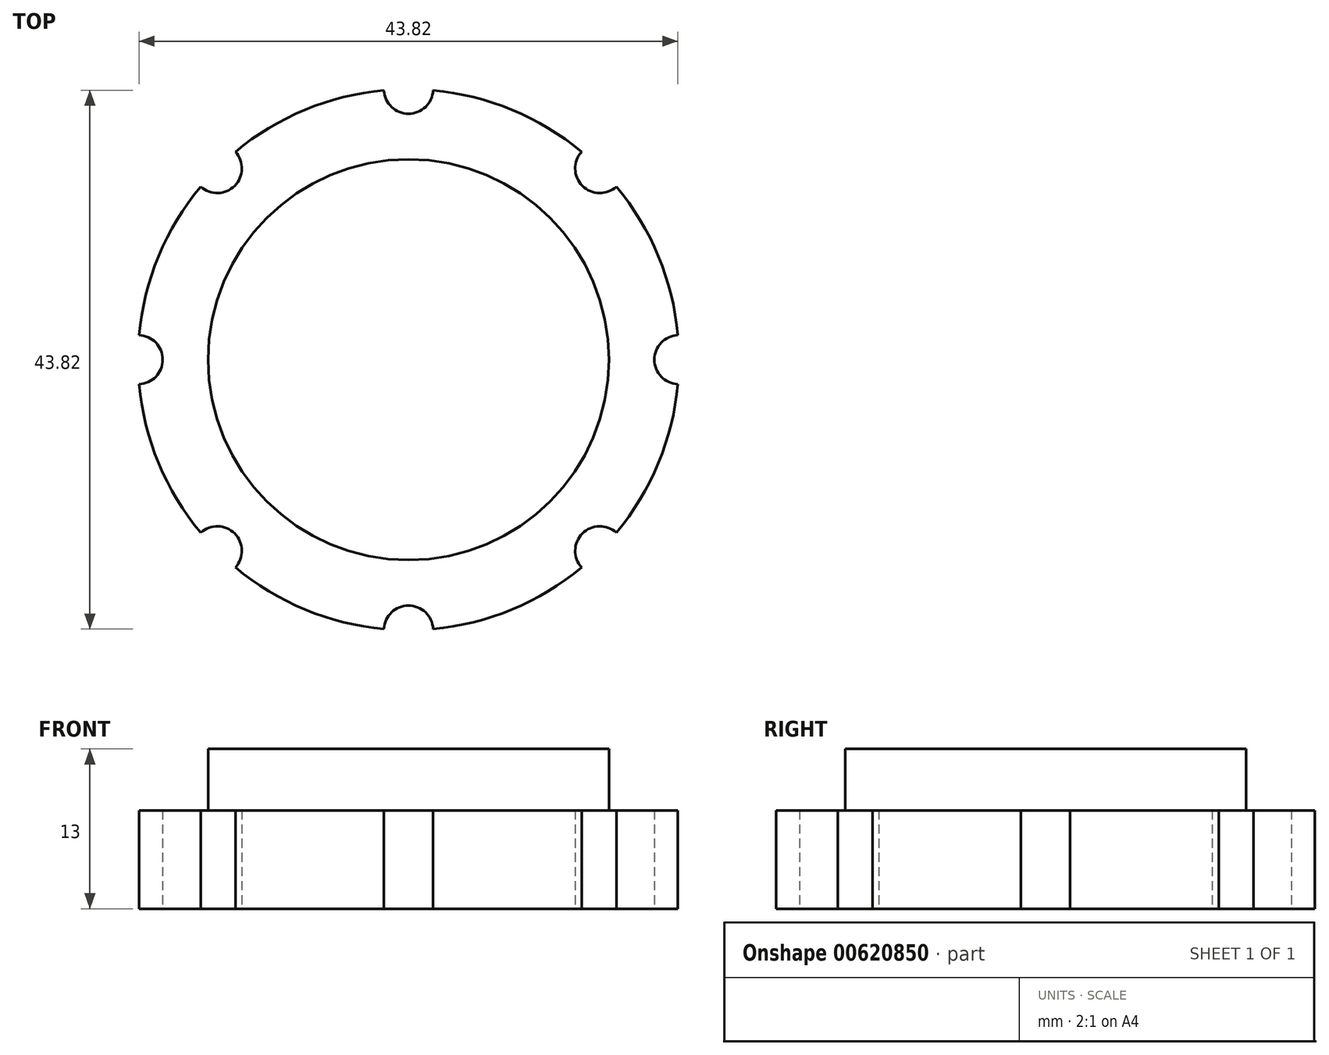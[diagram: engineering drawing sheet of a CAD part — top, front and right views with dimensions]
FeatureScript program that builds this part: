
annotation { "Feature Type Name" : "Feature", "Feature Type Description" : "" }
export const myFeature = defineFeature(function(context is Context, id is Id, definition is map)
    precondition{}
    {
        {
            var Q0;
            Q0=qCreatedBy(makeId("Top.planeOp"),FACE);
            var sketch = newSketch(context, id + "F0", { "sketchPlane" : qUnion([Q0])});
            skCircle(sketch, "E0", {"center": v(0, 0) * mm, "radius": 22 * mm});
            skSolve(sketch);
        }
        {
            var Q0;
            Q0 = qSketchRegion(id + "F0", true);
            extrude(context, id + "F1", {"entities" : qUnion([Q0]), "depth" : 8 * mm, "offsetDistance" : 25 * mm});
        }
        {
            var Q0;
            Q0=makeQuery(id+"F1.opExtrude","CAP_FACE",FACE,{"disambiguationData":[OSD([sQuery(id+"F0.wireOp",EDGE,"E0")])],"isStart":false});
            var sketch = newSketch(context, id + "F2", { "sketchPlane" : qUnion([Q0])});
            skCircle(sketch, "E1", {"center": v(0, 0) * mm, "radius": 16.3 * mm});
            skSolve(sketch);
        }
        {
            var Q0;
            Q0 = qSketchRegion(id + "F2", true);
            extrude(context, id + "F3", {"entities" : qUnion([Q0]), "operationType" : NewBodyOperationType.ADD, "depth" : 5 * mm, "offsetDistance" : 25 * mm});
        }
        {
            var Q0;
            Q0=makeQuery(id+"F1.opExtrude","CAP_FACE",FACE,{"disambiguationData":[OSD([sQuery(id+"F0.wireOp",EDGE,"E0")])],"isStart":true});
            var sketch = newSketch(context, id + "F4", { "sketchPlane" : qUnion([Q0])});
            skCircle(sketch, "E2", {"center": v(22, 0) * mm, "radius": 2 * mm});
            skCircle(sketch, "E3", {"center": v(15.56, -15.56) * mm, "radius": 2 * mm});
            skCircle(sketch, "E4", {"center": v(0, -22) * mm, "radius": 2 * mm});
            skCircle(sketch, "E5", {"center": v(-15.56, -15.56) * mm, "radius": 2 * mm});
            skCircle(sketch, "E6", {"center": v(-22, 0) * mm, "radius": 2 * mm});
            skCircle(sketch, "E7", {"center": v(-15.56, 15.56) * mm, "radius": 2 * mm});
            skCircle(sketch, "E8", {"center": v(0, 22) * mm, "radius": 2 * mm});
            skCircle(sketch, "E9", {"center": v(15.56, 15.56) * mm, "radius": 2 * mm});
            skSolve(sketch);
        }
        {
            var Q0;
            Q0 = qSketchRegion(id + "F4", true);
            extrude(context, id + "F5", {"entities" : qUnion([Q0]), "operationType" : NewBodyOperationType.REMOVE, "oppositeDirection" : true, "depth" : 25 * mm, "offsetDistance" : 25 * mm});
        }
    });
